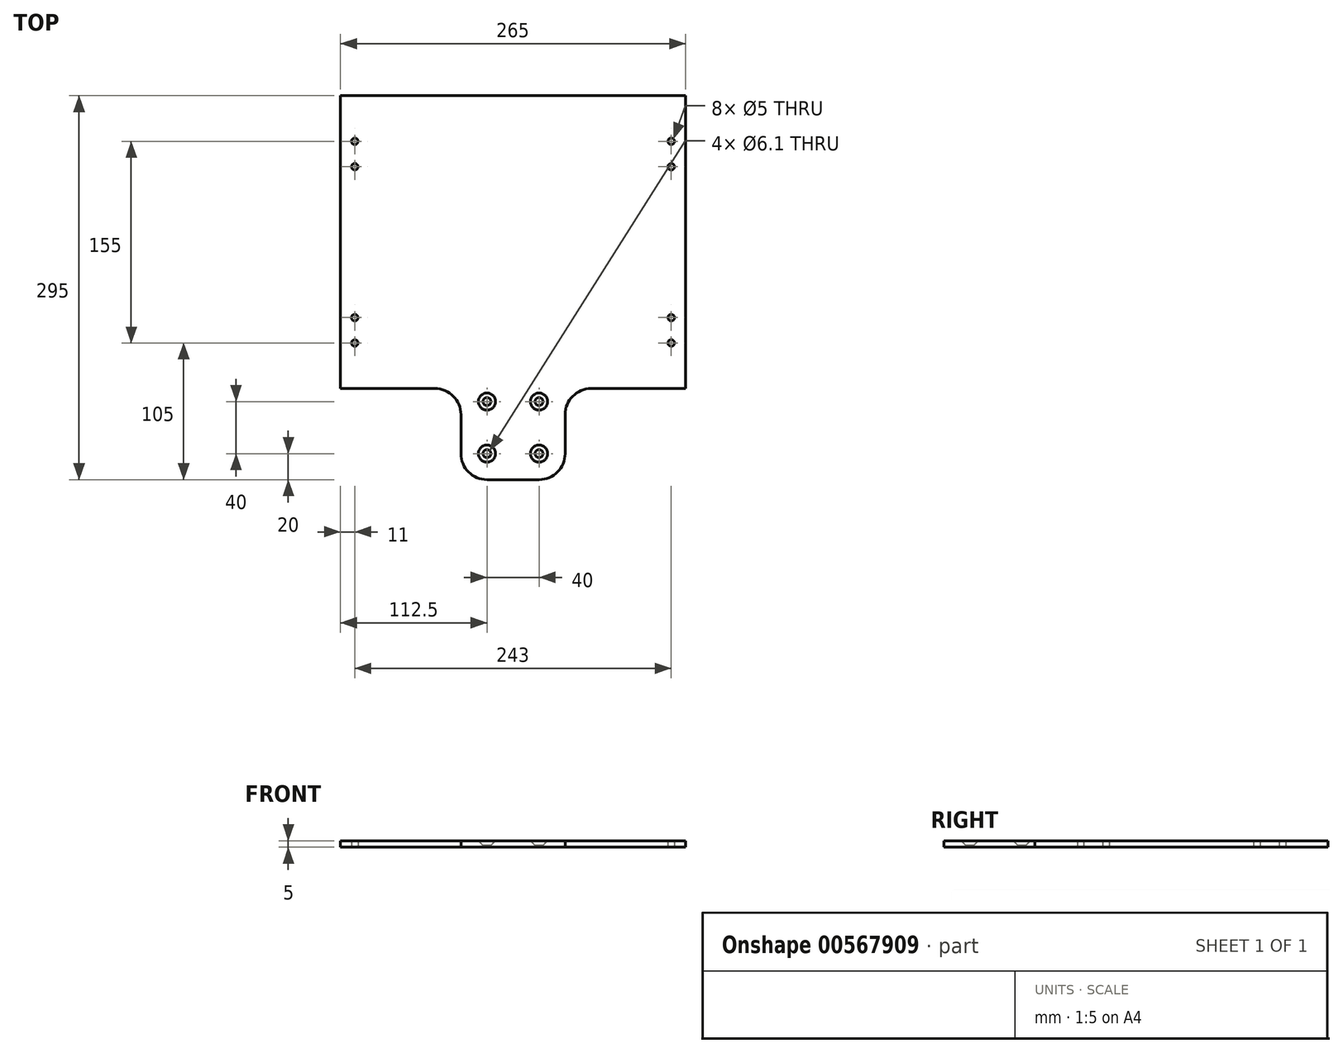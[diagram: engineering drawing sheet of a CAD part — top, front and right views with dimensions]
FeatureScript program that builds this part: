
annotation { "Feature Type Name" : "Feature", "Feature Type Description" : "" }
export const myFeature = defineFeature(function(context is Context, id is Id, definition is map)
    precondition{}
    {
        {
            var Q0;
            Q0=qCreatedBy(makeId("Top.planeOp"),FACE);
            var sketch = newSketch(context, id + "F0", { "sketchPlane" : qUnion([Q0])});
            skLineSegment(sketch, "E0.bottom", {"start": v(0, 0) * mm, "end": v(72.5, 0) * mm});
            skLineSegment(sketch, "E0.top", {"start": v(0, 225) * mm, "end": v(265, 225) * mm});
            skLineSegment(sketch, "E0.left", {"start": v(0, 0) * mm, "end": v(0, 225) * mm});
            skLineSegment(sketch, "E0.right", {"start": v(265, 0) * mm, "end": v(265, 225) * mm});
            skCircle(sketch, "E1", {"center": v(11, 54.5) * mm, "radius": 2.5 * mm});
            skCircle(sketch, "E2", {"center": v(11, 35) * mm, "radius": 2.5 * mm});
            skCircle(sketch, "E3", {"center": v(254, 54.5) * mm, "radius": 2.5 * mm});
            skCircle(sketch, "E4", {"center": v(254, 35) * mm, "radius": 2.5 * mm});
            skCircle(sketch, "E5", {"center": v(254, 190) * mm, "radius": 2.5 * mm});
            skCircle(sketch, "E6", {"center": v(254, 170.5) * mm, "radius": 2.5 * mm});
            skCircle(sketch, "E7", {"center": v(11, 190) * mm, "radius": 2.5 * mm});
            skCircle(sketch, "E8", {"center": v(11, 170.5) * mm, "radius": 2.5 * mm});
            skCircle(sketch, "E9", {"center": v(112.5, -10) * mm, "radius": 3.05 * mm});
            skCircle(sketch, "E10", {"center": v(152.5, -10) * mm, "radius": 3.05 * mm});
            skCircle(sketch, "E11", {"center": v(152.5, -50) * mm, "radius": 3.05 * mm});
            skCircle(sketch, "E12", {"center": v(112.5, -50) * mm, "radius": 3.05 * mm});
            skArc(sketch, "E13", {"start": v(92.5, -50) * mm, "mid": v(98.36, -64.14) * mm, "end": v(112.5, -70) * mm});
            skArc(sketch, "E14", {"start": v(152.5, -70) * mm, "mid": v(166.64, -64.14) * mm, "end": v(172.5, -50) * mm});
            skLineSegment(sketch, "E15", {"start": v(112.5, -70) * mm, "end": v(152.5, -70) * mm});
            skLineSegment(sketch, "E16", {"start": v(92.5, -50) * mm, "end": v(92.5, -20) * mm});
            skLineSegment(sketch, "E17", {"start": v(172.5, -50) * mm, "end": v(172.5, -20) * mm});
            skPoint(sketch, "E18", {"position": v(132.5, 0) * mm});
            skPoint(sketch, "E19", {"position": v(132.5, -70) * mm});
            skPoint(sketch, "E20", {"position": v(132.5, 225) * mm});
            skArc(sketch, "E21", {"start": v(92.5, -20) * mm, "mid": v(86.64, -5.86) * mm, "end": v(72.5, 0) * mm});
            skArc(sketch, "E22", {"start": v(192.5, 0) * mm, "mid": v(178.36, -5.86) * mm, "end": v(172.5, -20) * mm});
            skPoint(sketch, "E23.orphan", {"position": v(172.5, 0) * mm});
            skLineSegment(sketch, "E24.trimOffspring", {"start": v(192.5, 0) * mm, "end": v(265, 0) * mm});
            skPoint(sketch, "E25.orphan", {"position": v(92.5, 0) * mm});
            skPoint(sketch, "E26", {"position": v(21.92, 121.6) * mm});
            skSolve(sketch);
        }
        {
            var Q0;
            Q0=makeQuery(id+"F0.imprint","IMPRINT",FACE,{"disambiguationData":[TD([[makeQuery(id+"F0.imprint","IMPRINT",EDGE,{"derivedFrom":sQuery(id+"F0.wireOp",EDGE,"E0.bottom")}),1.0]])]});
            extrude(context, id + "F1", {"entities" : qUnion([Q0]), "depth" : 5 * mm, "offsetDistance" : 25 * mm});
        }
        {
            var Q0;
            Q0=makeQuery(id+"F1.opExtrude","CAP_EDGE",EDGE,{"disambiguationData":[OSD([sQuery(id+"F0.wireOp",EDGE,"E9")])],"isStart":false});
            var Q1;
            Q1=makeQuery(id+"F1.opExtrude","CAP_EDGE",EDGE,{"disambiguationData":[OSD([sQuery(id+"F0.wireOp",EDGE,"E10")])],"isStart":false});
            var Q2;
            Q2=makeQuery(id+"F1.opExtrude","CAP_EDGE",EDGE,{"disambiguationData":[OSD([sQuery(id+"F0.wireOp",EDGE,"E12")])],"isStart":false});
            var Q3;
            Q3=makeQuery(id+"F1.opExtrude","CAP_EDGE",EDGE,{"disambiguationData":[OSD([sQuery(id+"F0.wireOp",EDGE,"E11")])],"isStart":false});
            chamfer(context, id + "F2", {"entities" : qUnion([Q0, Q1, Q2, Q3]), "width" : 3.5 * mm, "tangentPropagation" : true});
        }
    });
